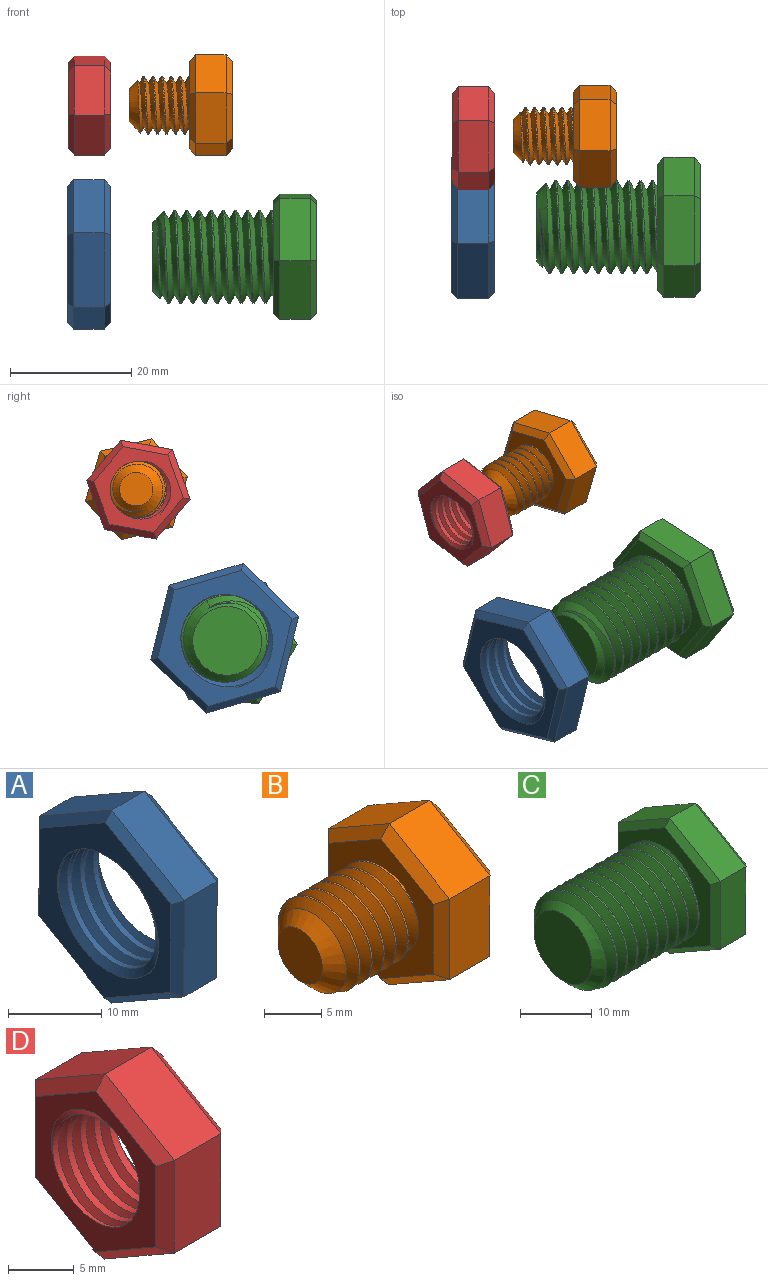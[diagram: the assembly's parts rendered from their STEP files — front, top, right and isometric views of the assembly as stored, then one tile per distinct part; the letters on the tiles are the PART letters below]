
ASSEMBLY  parts=4 mates=2
PART A: 23 faces, bbox 9.3x22.7x26 mm
  f0: cylinder r=7.24mm len=14.48mm, axis (1,0,0), area 111.6mm2, adj f7,f8,f21,f22
  f1: plane 10.98x6.38mm, normal (0,-0.5,0.86), area 63.5mm2, adj f2,f6,f14,f18
  f2: plane 12.7x5mm, normal (0,-1,0), area 63.5mm2, adj f1,f3,f12,f16
  f3: plane 11.02x6.32mm, normal (0,-0.5,-0.87), area 63.5mm2, adj f2,f4,f10,f15
  f4: plane 10.98x6.38mm, normal (0,0.5,-0.86), area 63.5mm2, adj f3,f5,f9,f17
  f5: plane 12.7x5mm, normal (0,1,0), area 63.5mm2, adj f4,f6,f11,f19
  f6: plane 11.02x6.32mm, normal (0,0.5,0.87), area 63.5mm2, adj f1,f5,f13,f20
  f7: plane 23.73x20.67mm, normal (-1,0,0), area 164.4mm2, adj f0,f9,f10,f11,f12,f13,f14,f21
  f8: plane 23.73x20.67mm, normal (1,0,0), area 164.4mm2, adj f0,f15,f16,f17,f18,f19,f20,f21
  f9: plane 10.99x6.96mm, normal (-0.71,0.36,-0.61), area 17.1mm2, adj f4,f7,f10,f11
  f10: plane 11.02x6.9mm, normal (-0.71,-0.35,-0.61), area 17.1mm2, adj f3,f7,f9,f12
  f11: plane 12.7x1.03mm, normal (-0.71,0.71,0), area 17.1mm2, adj f5,f7,f9,f13
  f12: plane 12.7x1.03mm, normal (-0.71,-0.71,0), area 17.1mm2, adj f2,f7,f10,f14
  f13: plane 11.02x6.9mm, normal (-0.71,0.35,0.61), area 17.1mm2, adj f6,f7,f11,f14
  f14: plane 10.99x6.96mm, normal (-0.71,-0.36,0.61), area 17.1mm2, adj f1,f7,f12,f13
  f15: plane 11.02x6.9mm, normal (0.71,-0.35,-0.61), area 17.1mm2, adj f3,f8,f16,f17
  f16: plane 12.7x1.03mm, normal (0.71,-0.71,0), area 17.1mm2, adj f2,f8,f15,f18
  f17: plane 10.99x6.96mm, normal (0.71,0.36,-0.61), area 17.1mm2, adj f4,f8,f15,f19
  f18: plane 10.99x6.96mm, normal (0.71,-0.36,0.61), area 17.1mm2, adj f1,f8,f16,f20
  f19: plane 12.7x1.03mm, normal (0.71,0.71,0), area 17.1mm2, adj f5,f8,f17,f20
  f20: plane 11.02x6.9mm, normal (0.71,0.35,0.61), area 17.1mm2, adj f6,f8,f18,f19
  f21: bspline ~19.31x16.73mm, area 223mm2, adj f0,f7,f8,f22
  f22: bspline ~19.31x16.73mm, area 223mm2, adj f0,f7,f8,f21
PART B: 25 faces, bbox 17.8x15.9x18.1 mm
  f0: cylinder r=4.75mm len=9.5mm, axis (1,0,0), area 28.1mm2, adj f1,f2,f4,f12
  f1: bspline ~10.97x9.91mm, area 196.7mm2, adj f0,f2,f4,f12
  f2: bspline ~10.97x10.66mm, area 196.6mm2, adj f0,f1,f4,f12
  f3: plane 5.5x5.5mm, normal (-1,0,0), area 23.8mm2, adj f4
  f4: cone r=4.75mm half-angle=45deg, axis (1,0,0), area 47.4mm2, adj f0,f1,f2,f3
  f5: plane 7.48x5mm, normal (0,-0.5,0.86), area 43.3mm2, adj f6,f10,f18,f22
  f6: plane 8.66x5mm, normal (0,-1,0), area 43.3mm2, adj f5,f7,f16,f20
  f7: plane 7.52x5mm, normal (0,-0.5,-0.87), area 43.3mm2, adj f6,f8,f14,f19
  f8: plane 7.48x5mm, normal (0,0.5,-0.86), area 43.3mm2, adj f7,f9,f13,f21
  f9: plane 8.66x5mm, normal (0,1,0), area 43.3mm2, adj f8,f10,f15,f23
  f10: plane 7.52x5mm, normal (0,0.5,0.87), area 43.3mm2, adj f5,f9,f17,f24
  f11: plane 15.01x13.03mm, normal (1,0,0), area 146.4mm2, adj f13,f14,f15,f16,f17,f18
  f12: plane 15.83x13.85mm, normal (-1,0,0), area 89.2mm2, adj f0,f1,f2,f19,f20,f21,f22,f23
  f13: plane 7.49x4.93mm, normal (0.71,0.36,-0.61), area 11.4mm2, adj f8,f11,f14,f15
  f14: plane 7.52x4.88mm, normal (0.71,-0.35,-0.61), area 11.4mm2, adj f7,f11,f13,f16
  f15: plane 8.66x1.03mm, normal (0.71,0.71,0), area 11.4mm2, adj f9,f11,f13,f17
  f16: plane 8.66x1.03mm, normal (0.71,-0.71,0), area 11.4mm2, adj f6,f11,f14,f18
  f17: plane 7.52x4.88mm, normal (0.71,0.35,0.61), area 11.4mm2, adj f10,f11,f15,f18
  f18: plane 7.49x4.93mm, normal (0.71,-0.36,0.61), area 11.4mm2, adj f5,f11,f16,f17
  f19: plane 7.52x4.88mm, normal (-0.71,-0.35,-0.61), area 11.4mm2, adj f7,f12,f20,f21
  f20: plane 8.66x1.03mm, normal (-0.71,-0.71,0), area 11.4mm2, adj f6,f12,f19,f22
  f21: plane 7.49x4.93mm, normal (-0.71,0.36,-0.61), area 11.4mm2, adj f8,f12,f19,f23
  f22: plane 7.49x4.93mm, normal (-0.71,-0.36,0.61), area 11.4mm2, adj f5,f12,f20,f24
  f23: plane 8.66x1.03mm, normal (-0.71,0.71,0), area 11.4mm2, adj f9,f12,f21,f24
  f24: plane 7.52x4.88mm, normal (-0.71,0.35,0.61), area 11.4mm2, adj f10,f12,f22,f23
PART C: 26 faces, bbox 27.7x20x23.1 mm
  f0: cylinder r=7.68mm len=18mm, axis (1,0,0), area 139.1mm2, adj f1,f2,f5,f13
  f1: bspline ~20.88x17.74mm, area 713.8mm2, adj f0,f2,f4,f5,f13
  f2: bspline ~21.88x17.74mm, area 715.1mm2, adj f0,f1,f4,f5,f13
  f3: plane 11.36x11.36mm, normal (-1,0,0), area 101.4mm2, adj f4
  f4: cone r=7.68mm half-angle=45deg, axis (1,0,0), area 63.2mm2, adj f1,f2,f3,f5
  f5: cone r=7.68mm half-angle=45deg, axis (1,0,0), area 13.2mm2, adj f0,f1,f2,f4
  f6: plane 9.98x5.81mm, normal (0,-0.5,0.86), area 57.7mm2, adj f7,f11,f19,f23
  f7: plane 11.55x5mm, normal (0,-1,0), area 57.7mm2, adj f6,f8,f17,f21
  f8: plane 10.02x5.74mm, normal (0,-0.5,-0.87), area 57.7mm2, adj f7,f9,f15,f20
  f9: plane 9.98x5.81mm, normal (0,0.5,-0.86), area 57.7mm2, adj f8,f10,f14,f22
  f10: plane 11.55x5mm, normal (0,1,0), area 57.7mm2, adj f9,f11,f16,f24
  f11: plane 10.02x5.74mm, normal (0,0.5,0.87), area 57.7mm2, adj f6,f10,f18,f25
  f12: plane 20.78x18.04mm, normal (1,0,0), area 280.6mm2, adj f14,f15,f16,f17,f18,f19
  f13: plane 20.78x18.04mm, normal (-1,0,0), area 125.2mm2, adj f0,f1,f2,f20,f21,f22,f23,f24
  f14: plane 9.98x6.38mm, normal (0.71,0.36,-0.61), area 15.5mm2, adj f9,f12,f15,f16
  f15: plane 10.02x6.32mm, normal (0.71,-0.35,-0.61), area 15.5mm2, adj f8,f12,f14,f17
  f16: plane 11.55x1.04mm, normal (0.71,0.71,0), area 15.5mm2, adj f10,f12,f14,f18
  f17: plane 11.55x1.04mm, normal (0.71,-0.71,0), area 15.5mm2, adj f7,f12,f15,f19
  f18: plane 10.02x6.32mm, normal (0.71,0.35,0.61), area 15.5mm2, adj f11,f12,f16,f19
  f19: plane 9.98x6.38mm, normal (0.71,-0.36,0.61), area 15.5mm2, adj f6,f12,f17,f18
  f20: plane 10.02x6.32mm, normal (-0.71,-0.35,-0.61), area 15.5mm2, adj f8,f13,f21,f22
  f21: plane 11.55x1.04mm, normal (-0.71,-0.71,0), area 15.5mm2, adj f7,f13,f20,f23
  f22: plane 9.98x6.38mm, normal (-0.71,0.36,-0.61), area 15.5mm2, adj f9,f13,f20,f24
  f23: plane 9.98x6.38mm, normal (-0.71,-0.36,0.61), area 15.5mm2, adj f6,f13,f21,f25
  f24: plane 11.55x1.04mm, normal (-0.71,0.71,0), area 15.5mm2, adj f10,f13,f22,f25
  f25: plane 10.02x6.32mm, normal (-0.71,0.35,0.61), area 15.5mm2, adj f11,f13,f23,f24
PART D: 23 faces, bbox 9.1x15.4x17.7 mm
  f0: plane 7.49x5mm, normal (0,-0.5,0.86), area 43.3mm2, adj f1,f5,f13,f17
  f1: plane 8.66x5mm, normal (0,-1,0), area 43.3mm2, adj f0,f2,f11,f15
  f2: plane 7.51x5mm, normal (0,-0.5,-0.87), area 43.3mm2, adj f1,f3,f9,f14
  f3: plane 7.49x5mm, normal (0,0.5,-0.86), area 43.3mm2, adj f2,f4,f8,f16
  f4: plane 8.66x5mm, normal (0,1,0), area 43.3mm2, adj f3,f5,f10,f18
  f5: plane 7.51x5mm, normal (0,0.5,0.87), area 43.3mm2, adj f0,f4,f12,f19
  f6: plane 15.37x13.38mm, normal (-1,0,0), area 71.4mm2, adj f8,f9,f10,f11,f12,f13,f20,f21
  f7: plane 15.37x13.38mm, normal (1,0,0), area 71.4mm2, adj f14,f15,f16,f17,f18,f19,f20,f21
  f8: plane 7.49x4.93mm, normal (-0.71,0.36,-0.61), area 11.4mm2, adj f3,f6,f9,f10
  f9: plane 7.51x4.89mm, normal (-0.71,-0.35,-0.61), area 11.4mm2, adj f2,f6,f8,f11
  f10: plane 8.66x1.02mm, normal (-0.71,0.71,0), area 11.4mm2, adj f4,f6,f8,f12
  f11: plane 8.66x1.02mm, normal (-0.71,-0.71,0), area 11.4mm2, adj f1,f6,f9,f13
  f12: plane 7.51x4.89mm, normal (-0.71,0.35,0.61), area 11.4mm2, adj f5,f6,f10,f13
  f13: plane 7.49x4.93mm, normal (-0.71,-0.36,0.61), area 11.4mm2, adj f0,f6,f11,f12
  f14: plane 7.51x4.89mm, normal (0.71,-0.35,-0.61), area 11.4mm2, adj f2,f7,f15,f16
  f15: plane 8.66x1.02mm, normal (0.71,-0.71,0), area 11.4mm2, adj f1,f7,f14,f17
  f16: plane 7.49x4.93mm, normal (0.71,0.36,-0.61), area 11.4mm2, adj f3,f7,f14,f18
  f17: plane 7.49x4.93mm, normal (0.71,-0.36,0.61), area 11.4mm2, adj f0,f7,f15,f19
  f18: plane 8.66x1.02mm, normal (0.71,0.71,0), area 11.4mm2, adj f4,f7,f16,f19
  f19: plane 7.51x4.89mm, normal (0.71,0.35,0.61), area 11.4mm2, adj f5,f7,f17,f18
  f20: cylinder r=4.66mm len=9.32mm, axis (1,0,0), area 85.4mm2, adj f6,f7,f21,f22
  f21: bspline ~12.5x10.82mm, area 128.4mm2, adj f6,f7,f20,f22
  f22: bspline ~12.5x10.82mm, area 128.5mm2, adj f6,f7,f20,f21
PLACE A rot(axis=(0,0.6,-0.8),180deg) t=(-55.27,-6.86,23.48)mm fixed
PLACE B rot(axis=(-1,0,0),43.8deg) t=(-31.66,7.73,48.08)mm
PLACE C rot(axis=(1,0,0),153.1deg) t=(-17.77,-7.25,23.06)mm
PLACE D rot(axis=(1,0,0),100.2deg) t=(-48.16,7.38,48.02)mm fixed
MATE cylindrical C.f0 <-> A.f7  axis (-1,0,0) through (-41.27,-7.25,23.06)mm
MATE cylindrical B.f0 <-> D.f6  axis (-1,0,0) through (-45.16,7.73,48.08)mm
